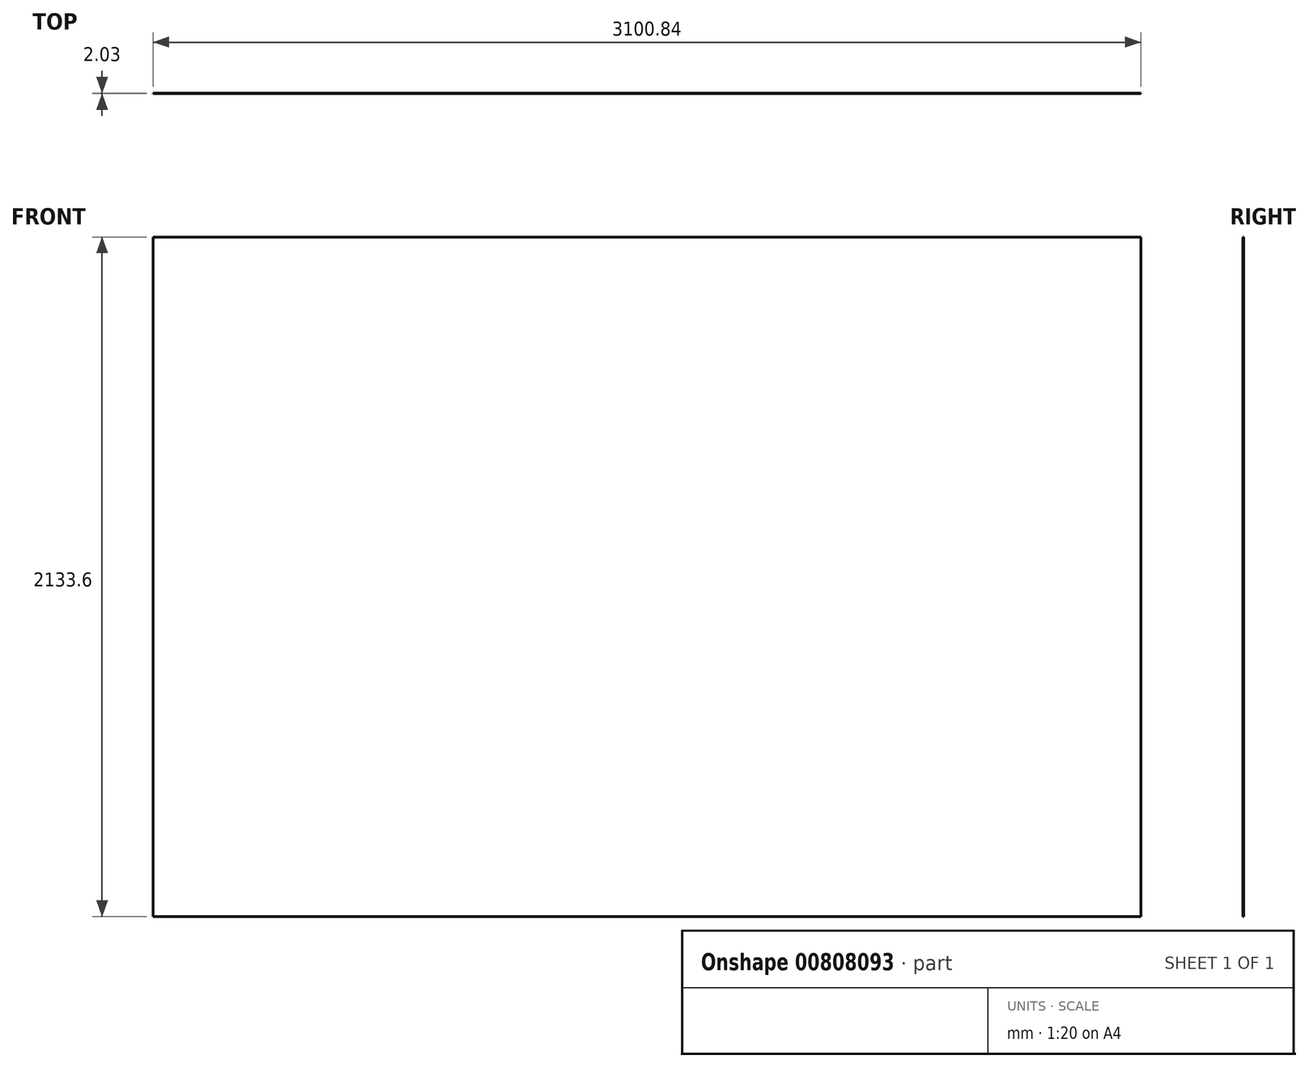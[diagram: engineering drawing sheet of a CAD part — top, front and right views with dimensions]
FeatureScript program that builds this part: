
annotation { "Feature Type Name" : "Feature", "Feature Type Description" : "" }
export const myFeature = defineFeature(function(context is Context, id is Id, definition is map)
    precondition{}
    {
        {
            var Q0;
            Q0=qCreatedBy(makeId("Front.planeOp"),FACE);
            var sketch = newSketch(context, id + "F0", { "sketchPlane" : qUnion([Q0])});
            skLineSegment(sketch, "E0.bottom", {"start": v(-2409.49, 314.8) * mm, "end": v(691.35, 314.8) * mm});
            skLineSegment(sketch, "E0.top", {"start": v(-2409.49, -1818.8) * mm, "end": v(691.35, -1818.8) * mm});
            skLineSegment(sketch, "E0.left", {"start": v(-2409.49, 314.8) * mm, "end": v(-2409.49, -1818.8) * mm});
            skLineSegment(sketch, "E0.right", {"start": v(691.35, 314.8) * mm, "end": v(691.35, -1818.8) * mm});
            skSolve(sketch);
        }
        {
            var Q0;
            Q0=qSketchRegion(id+"F0",true);
            extrude(context, id + "F1", {"entities" : qUnion([Q0]), "depth" : 2.03 * mm, "offsetDistance" : 25.4 * mm});
        }
    });
